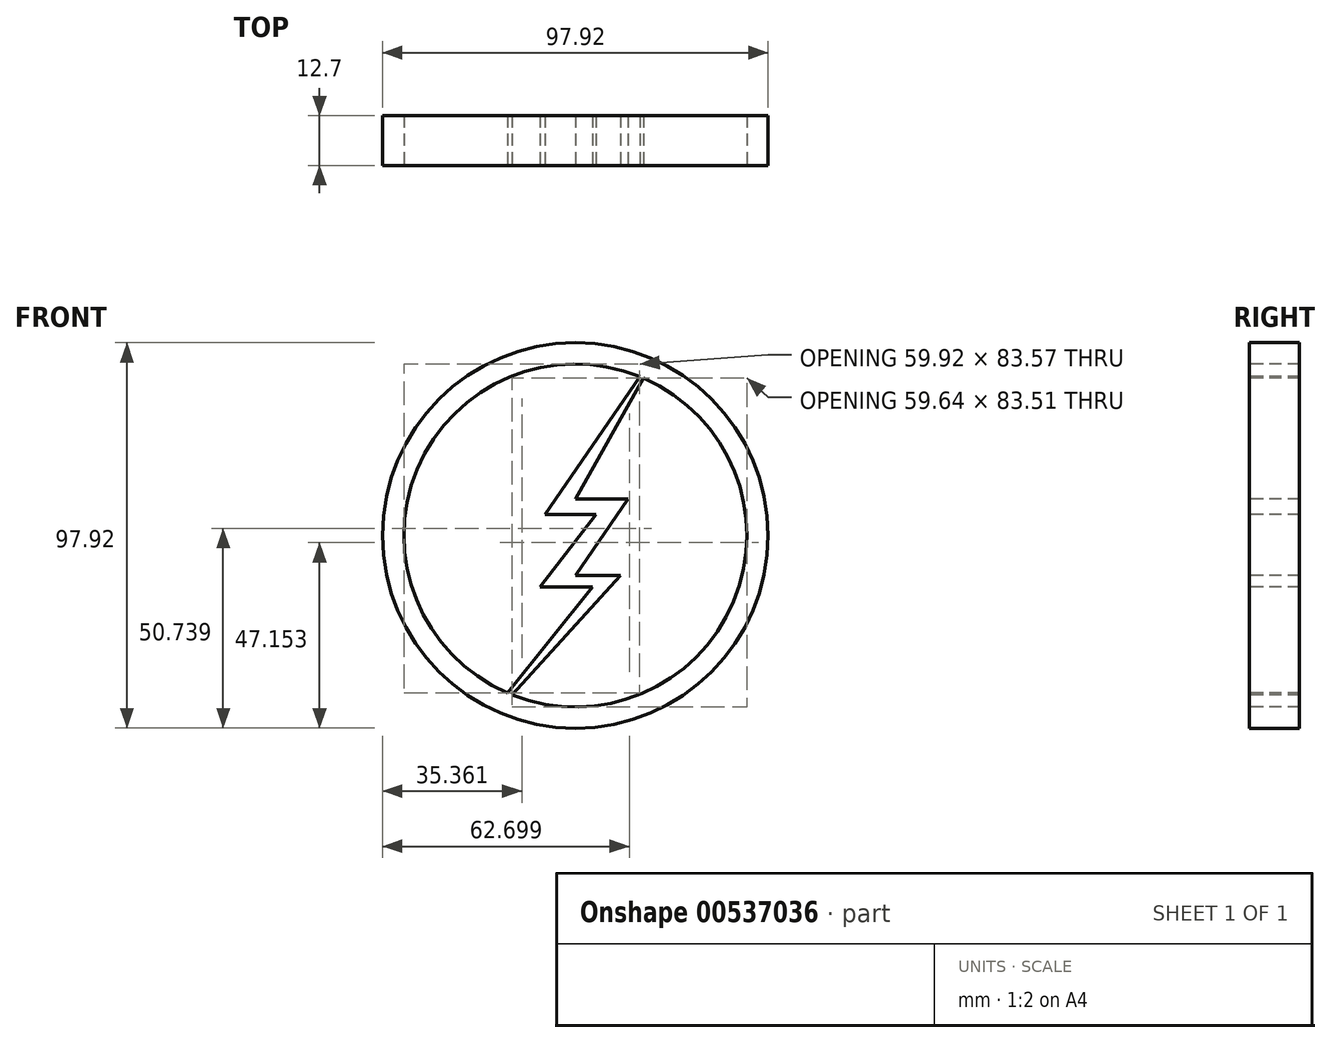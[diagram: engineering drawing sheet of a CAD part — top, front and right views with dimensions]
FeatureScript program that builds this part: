
annotation { "Feature Type Name" : "Feature", "Feature Type Description" : "" }
export const myFeature = defineFeature(function(context is Context, id is Id, definition is map)
    precondition{}
    {
        {
            var Q0;
            Q0=qCreatedBy(makeId("Front.planeOp"),FACE);
            var sketch = newSketch(context, id + "F0", { "sketchPlane" : qUnion([Q0])});
            skCircle(sketch, "E0", {"center": v(0, 0) * mm, "radius": 48.96 * mm});
            skSolve(sketch);
        }
        {
            var Q0;
            Q0=makeQuery(id+"F0.imprint","IMPRINT",FACE,{"disambiguationData":[TD([[makeQuery(id+"F0.imprint","IMPRINT",EDGE,{"derivedFrom":sQuery(id+"F0.wireOp",EDGE,"E0")}),1.0]])]});
            extrude(context, id + "F1", {"entities" : qUnion([Q0]), "depth" : 12.7 * mm, "offsetDistance" : 25.4 * mm});
        }
        {
            var Q0;
            Q0=makeQuery(id+"F1.opExtrude","CAP_FACE",FACE,{"disambiguationData":[OSD([sQuery(id+"F0.wireOp",EDGE,"E0")])],"isStart":false});
            var sketch = newSketch(context, id + "F2", { "sketchPlane" : qUnion([Q0])});
            skCircle(sketch, "E1", {"center": v(0, 0) * mm, "radius": 43.56 * mm});
            skSolve(sketch);
        }
        {
            var Q0;
            Q0=makeQuery(id+"F2.imprint","IMPRINT",FACE,{"disambiguationData":[TD([[makeQuery(id+"F2.imprint","IMPRINT",EDGE,{"derivedFrom":sQuery(id+"F2.wireOp",EDGE,"E1")}),1.0]])]});
            extrude(context, id + "F3", {"entities" : qUnion([Q0]), "operationType" : NewBodyOperationType.REMOVE, "oppositeDirection" : true, "depth" : 12.7 * mm, "offsetDistance" : 25.4 * mm});
        }
        {
            var Q0;
            Q0=makeQuery(id+"F1.opExtrude","CAP_FACE",FACE,{"disambiguationData":[OSD([sQuery(id+"F0.wireOp",EDGE,"E0")])],"isStart":false});
            var sketch = newSketch(context, id + "F4", { "sketchPlane" : qUnion([Q0])});
            skLineSegment(sketch, "E2", {"start": v(23.57, 50.86) * mm, "end": v(-7.75, 5.27) * mm});
            skLineSegment(sketch, "E3", {"start": v(-7.75, 5.27) * mm, "end": v(5.27, 5.27) * mm});
            skLineSegment(sketch, "E4", {"start": v(5.27, 5.27) * mm, "end": v(-9, -13.02) * mm});
            skLineSegment(sketch, "E5", {"start": v(-9, -13.02) * mm, "end": v(4.34, -13.02) * mm});
            skLineSegment(sketch, "E6", {"start": v(4.34, -13.02) * mm, "end": v(-29.15, -54.9) * mm});
            skLineSegment(sketch, "E7", {"start": v(23.57, 50.86) * mm, "end": v(0, 9.3) * mm});
            skLineSegment(sketch, "E8", {"start": v(0, 9.3) * mm, "end": v(13.33, 9.3) * mm});
            skLineSegment(sketch, "E9", {"start": v(13.33, 9.3) * mm, "end": v(0, -10.1) * mm});
            skLineSegment(sketch, "E10", {"start": v(0, -10.1) * mm, "end": v(11.47, -10.1) * mm});
            skLineSegment(sketch, "E11", {"start": v(11.47, -10.1) * mm, "end": v(-29.15, -54.9) * mm});
            skSolve(sketch);
        }
        {
            var Q0;
            {var subQ7=sQuery(id+"F4.wireOp",EDGE,"E3");Q0=makeQuery(id+"F4.imprint","IMPRINT",FACE,{"disambiguationData":[TD([[makeQuery(id+"F4.imprint","IMPRINT",EDGE,{"derivedFrom":subQ7}),1.0]])]});}
            extrude(context, id + "F5", {"entities" : qUnion([Q0]), "operationType" : NewBodyOperationType.ADD, "oppositeDirection" : true, "depth" : 12.7 * mm, "offsetDistance" : 25.4 * mm});
        }
    });
